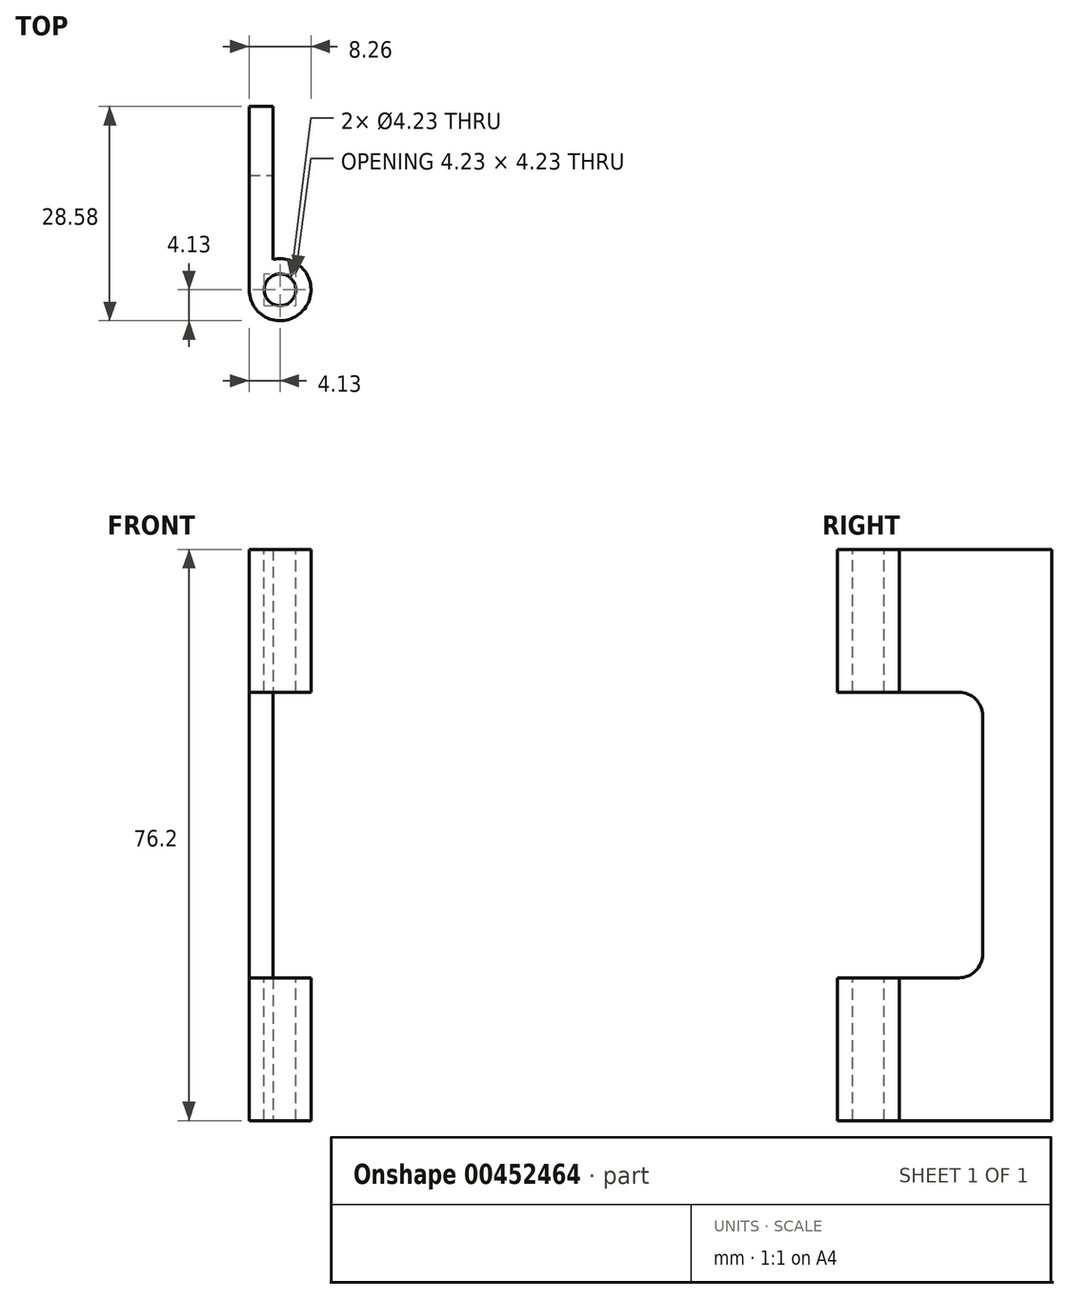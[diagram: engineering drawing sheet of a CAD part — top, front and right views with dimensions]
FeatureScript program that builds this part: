
annotation { "Feature Type Name" : "Feature", "Feature Type Description" : "" }
export const myFeature = defineFeature(function(context is Context, id is Id, definition is map)
    precondition{}
    {
        {
            var Q0;
            Q0=qCreatedBy(makeId("Top.planeOp"),FACE);
            var sketch = newSketch(context, id + "F0", { "sketchPlane" : qUnion([Q0])});
            skLineSegment(sketch, "E0", {"start": v(-0.95, 24.45) * mm, "end": v(-4.13, 24.45) * mm});
            skArc(sketch, "E1", {"start": v(-4.13, 0) * mm, "mid": v(3.24, -2.56) * mm, "end": v(-0.95, 4.02) * mm});
            skLineSegment(sketch, "E2", {"start": v(-4.13, 24.45) * mm, "end": v(-4.13, 0) * mm});
            skLineSegment(sketch, "E3.0", {"start": v(-0.95, 24.45) * mm, "end": v(-0.95, 4.02) * mm});
            skSolve(sketch);
        }
        {
            var Q0;
            Q0=qSketchRegion(id+"F0",true);
            extrude(context, id + "F1", {"entities" : qUnion([Q0]), "endBound" : BoundingType.SYMMETRIC, "depth" : 76.2 * mm});
        }
        {
            var Q0;
            Q0=makeQuery(id+"F1.opExtrude","CAP_FACE",FACE,{"disambiguationData":[OSD([sQuery(id+"F0.wireOp",EDGE,"E0"),sQuery(id+"F0.wireOp",EDGE,"NAVHtsbN-CQDX-7JxZ-XKDg-LEJrFOI6qL6S"),sQuery(id+"F0.wireOp",EDGE,"abe97878-674e-4916-bdfa-e1939a1c8ff60.MirrorCS"),sQuery(id+"F0.wireOp",EDGE,"85760476-aab7-44b0-82d2-3e1560c6169b.0"),sQuery(id+"F0.wireOp",EDGE,"027a6a38-1eb0-4f24-81a0-5b27cf7d5e49.0"),sQuery(id+"F0.wireOp",EDGE,"E1")])],"isStart":false});
            var sketch = newSketch(context, id + "F2", { "sketchPlane" : qUnion([Q0])});
            skPoint(sketch, "E4", {"position": v(0, 0) * mm});
            skSolve(sketch);
        }
        {
            var Q0;
            Q0=sQuery(id+"F2.wireOp",VERTEX,"E4");
            var Q1;
            Q1=makeQuery(id+"F1.opExtrude","SWEPT_BODY",BODY,{"disambiguationData":[OSD([sQuery(id+"F0.wireOp",EDGE,"E0"),sQuery(id+"F0.wireOp",EDGE,"NAVHtsbN-CQDX-7JxZ-XKDg-LEJrFOI6qL6S"),sQuery(id+"F0.wireOp",EDGE,"abe97878-674e-4916-bdfa-e1939a1c8ff60.MirrorCS"),sQuery(id+"F0.wireOp",EDGE,"85760476-aab7-44b0-82d2-3e1560c6169b.0"),sQuery(id+"F0.wireOp",EDGE,"027a6a38-1eb0-4f24-81a0-5b27cf7d5e49.0"),sQuery(id+"F0.wireOp",EDGE,"E1")])]});
            hole(context, id + "F3", {"style" : HoleStyle.SIMPLE, "endStyle" : HoleEndStyle.THROUGH, "holeDiameter" : 4.23 * mm, "isTappedThrough" : true, "tappedDepth" : 12.7 * mm, "tapClearance" : 3, "locations" : qUnion([Q0]), "scope" : qUnion([Q1])});
        }
        {
            var Q0;
            Q0=makeQuery(id+"F1.opExtrude","SWEPT_FACE",FACE,{"disambiguationData":[OSD([sQuery(id+"F0.wireOp",EDGE,"E3.0")])]});
            var sketch = newSketch(context, id + "F4", { "sketchPlane" : qUnion([Q0])});
            skLineSegment(sketch, "E5", {"start": v(-4.13, 19.05) * mm, "end": v(15.24, 19.05) * mm});
            skLineSegment(sketch, "E6.MirrorCS", {"start": v(-4.13, -19.05) * mm, "end": v(15.24, -19.05) * mm});
            skLineSegment(sketch, "E7", {"start": v(15.24, 19.05) * mm, "end": v(15.24, -19.05) * mm});
            skLineSegment(sketch, "E8", {"start": v(-4.13, -19.05) * mm, "end": v(-4.13, 19.05) * mm});
            skSolve(sketch);
        }
        {
            var Q0;
            Q0 = qSketchRegion(id + "F4", true);
            extrude(context, id + "F5", {"entities" : qUnion([Q0]), "operationType" : NewBodyOperationType.REMOVE, "endBound" : BoundingType.SYMMETRIC, "oppositeDirection" : true, "depth" : 25.4 * mm});
        }
        {
            var Q0;
            Q0=makeQuery(id+"F5.boolean.opBoolean","COPY",EDGE,{"derivedFrom":makeQuery(id+"F5.opExtrude","SWEPT_EDGE",EDGE,{"disambiguationData":[OSD([sQuery(id+"F4.wireOp",EDGE,"E5"),sQuery(id+"F4.wireOp",EDGE,"E7")])]})});
            var Q1;
            Q1=makeQuery(id+"F5.boolean.opBoolean","COPY",EDGE,{"derivedFrom":makeQuery(id+"F5.opExtrude","SWEPT_EDGE",EDGE,{"disambiguationData":[OSD([sQuery(id+"F4.wireOp",EDGE,"E6.MirrorCS"),sQuery(id+"F4.wireOp",EDGE,"E7")])]})});
            fillet(context, id + "F6", {"entities" : qUnion([Q0, Q1]), "radius" : 3.17 * mm, "tangentPropagation" : true, "allowEdgeOverflow" : false});
        }
    });
